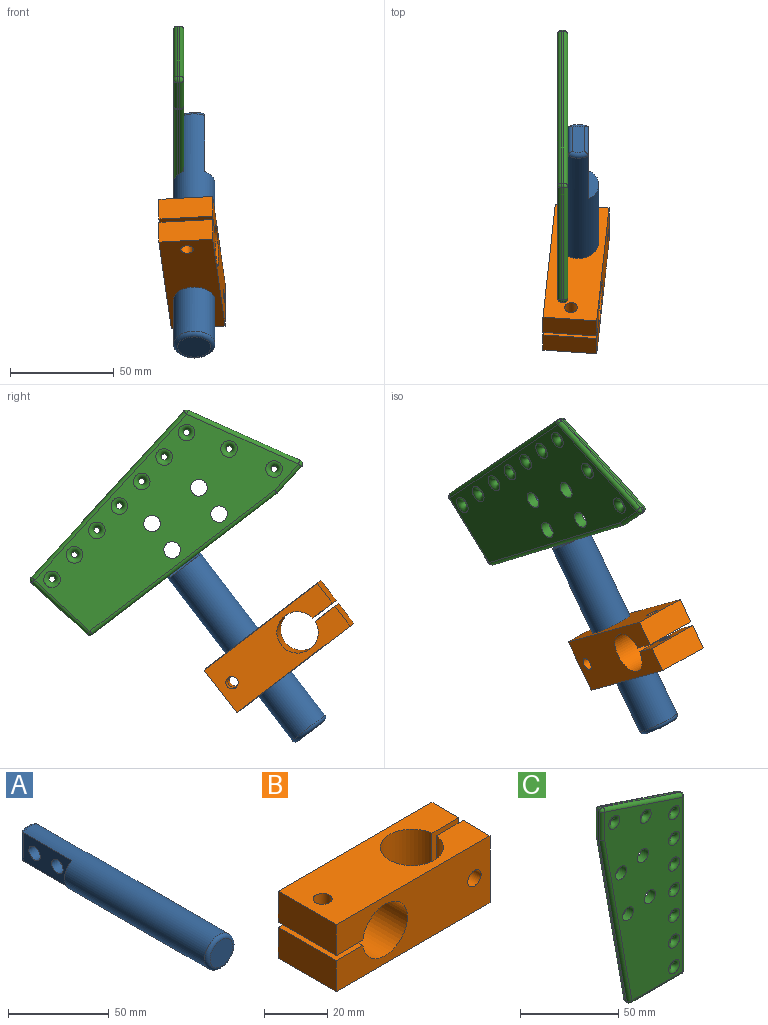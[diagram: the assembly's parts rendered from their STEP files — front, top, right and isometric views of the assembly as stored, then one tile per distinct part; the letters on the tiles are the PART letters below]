
ASSEMBLY  parts=3 mates=2
PART A: 14 faces, bbox 21.6x136x21.6 mm
  f0: plane 17.32x5mm, normal (0,1,0), area 61.4mm2, adj f1,f5
  f1: cylinder r=10mm len=132mm, axis (0,1,0), area 6869.6mm2, adj f0,f3,f4,f5,f9,f12,f13
  f2: plane 16x16mm, normal (0,-1,0), area 201.1mm2, adj f13
  f3: plane 17.32x5mm, normal (0,1,0), area 61.4mm2, adj f1,f4
  f4: plane 34x17.32mm, normal (-1,0,0), area 488.4mm2, adj f1,f3,f7,f8,f10
  f5: plane 34x17.32mm, normal (1,0,0), area 488.4mm2, adj f0,f1,f7,f8,f11
  f6: plane 16x6mm, normal (0,1,0), area 93.7mm2, adj f9,f10,f11,f12
  f7: cylinder r=4mm len=10mm, axis (-1,0,0), area 251.3mm2, adj f4,f5
  f8: cylinder r=4mm len=10mm, axis (-1,0,0), area 251.3mm2, adj f4,f5
  f9: torus R=8mm, axis (0,-1,0), area 27.9mm2, adj f1,f6,f10,f11
  f10: cylinder r=2mm len=17.32mm, axis (0,0,1), area 51.7mm2, adj f4,f6,f9,f12
  f11: cylinder r=2mm len=17.32mm, axis (0,0,-1), area 51.7mm2, adj f5,f6,f9,f12
  f12: torus R=8mm, axis (0,-1,0), area 27.9mm2, adj f1,f6,f10,f11
  f13: torus R=8mm, axis (0,-1,0), area 183mm2, adj f1,f2
PART B: 18 faces, bbox 69x26x26 mm
  f0: plane 26x12mm, normal (1,0,0), area 312mm2, adj f2,f8,f11,f15
  f1: cylinder r=3mm len=12mm, axis (0,1,0), area 226.2mm2, adj f11,f15
  f2: plane 69x26mm, normal (0,0,1), area 1427.5mm2, adj f0,f3,f9,f11,f12,f13,f14,f15
  f3: plane 26x12mm, normal (-1,0,0), area 312mm2, adj f2,f4,f11,f12
  f4: plane 26x12.05mm, normal (0,0,-1), area 285mm2, adj f3,f5,f11,f12,f17
  f5: cylinder r=10mm len=26mm, axis (0,1,0), area 1581.5mm2, adj f4,f6,f11,f12
  f6: plane 26x12.05mm, normal (0,0,1), area 285mm2, adj f5,f7,f11,f12,f16
  f7: plane 26x12mm, normal (-1,0,0), area 312mm2, adj f6,f8,f11,f12
  f8: plane 69x26mm, normal (0,0,-1), area 1427.5mm2, adj f0,f7,f9,f11,f12,f13,f14,f15
  f9: plane 26x12mm, normal (1,0,0), area 312mm2, adj f2,f8,f12,f14
  f10: cylinder r=3mm len=12mm, axis (0,1,0), area 226.2mm2, adj f12,f14
  f11: plane 69x26mm, normal (0,-1,0), area 1427.5mm2, adj f0,f1,f2,f3,f4,f5,f6,f7
  f12: plane 69x26mm, normal (0,1,0), area 1427.5mm2, adj f2,f3,f4,f5,f6,f7,f8,f9
  f13: cylinder r=10mm len=26mm, axis (0,0,1), area 1581.5mm2, adj f2,f8,f14,f15
  f14: plane 26x12.05mm, normal (0,-1,0), area 285mm2, adj f2,f8,f9,f10,f13
  f15: plane 26x12.05mm, normal (0,1,0), area 285mm2, adj f0,f1,f2,f8,f13
  f16: cylinder r=3mm len=12mm, axis (0,0,1), area 226.2mm2, adj f6,f8
  f17: cylinder r=3mm len=12mm, axis (0,0,1), area 226.2mm2, adj f2,f4
PART C: 45 faces, bbox 60x5x131.2 mm
  f0: plane 108.56x1mm, normal (1,0,0), area 108.6mm2, adj f20,f21,f22,f23
  f1: plane 56x18.67mm, normal (0.32,0,0.95), area 59mm2, adj f23,f28,f32,f33
  f2: plane 17.05x1mm, normal (-1,0,0), area 17mm2, adj f33,f38,f41,f44
  f3: plane 110.18x19.67mm, normal (-0.98,0,-0.18), area 111.9mm2, adj f30,f39,f40,f44
  f4: cylinder r=4mm len=8mm, axis (0,1,0), area 125.7mm2, adj f9,f10
  f5: cylinder r=4mm len=8mm, axis (0,1,0), area 125.7mm2, adj f9,f10
  f6: cylinder r=4mm len=8mm, axis (0,1,0), area 125.7mm2, adj f9,f10
  f7: cylinder r=4mm len=8mm, axis (0,1,0), area 125.7mm2, adj f9,f10
  f8: plane 36.33x1mm, normal (0,0,-1), area 36.3mm2, adj f21,f29,f30,f31
  f9: plane 127.23x56mm, normal (0,-1,0), area 4864.7mm2, adj f4,f5,f6,f7,f11,f12,f13,f14
  f10: plane 127.23x56mm, normal (0,1,0), area 4864.7mm2, adj f4,f5,f6,f7,f11,f12,f13,f14
  f11: torus R=4mm, axis (0,-1,0), area 118.9mm2, adj f9,f10
  f12: torus R=4mm, axis (0,-1,0), area 118.9mm2, adj f9,f10
  f13: torus R=4mm, axis (0,-1,0), area 118.9mm2, adj f9,f10
  f14: torus R=4mm, axis (0,-1,0), area 118.9mm2, adj f9,f10
  f15: torus R=4mm, axis (0,-1,0), area 118.9mm2, adj f9,f10
  f16: torus R=4mm, axis (0,-1,0), area 118.9mm2, adj f9,f10
  f17: torus R=4mm, axis (0,-1,0), area 118.9mm2, adj f9,f10
  f18: torus R=4mm, axis (0,-1,0), area 118.9mm2, adj f9,f10
  f19: torus R=4mm, axis (0,-1,0), area 118.9mm2, adj f9,f10
  f20: cylinder r=2mm len=108.56mm, axis (0,0,-1), area 341mm2, adj f0,f9,f24,f25
  f21: cylinder r=2mm len=2mm, axis (0,-1,0), area 3.1mm2, adj f0,f8,f25,f26
  f22: cylinder r=2mm len=108.56mm, axis (0,0,1), area 341mm2, adj f0,f10,f26,f27
  f23: cylinder r=2mm len=1.9mm, axis (0,1,0), area 2.5mm2, adj f0,f1,f24,f27
  f24: sphere r=2mm, area 5mm2, adj f20,f23,f28
  f25: sphere r=2mm, area 6.3mm2, adj f20,f21,f29
  f26: sphere r=2mm, area 6.3mm2, adj f21,f22,f31
  f27: sphere r=2mm, area 5mm2, adj f22,f23,f32
  f28: cylinder r=2mm len=56.63mm, axis (0.95,0,-0.32), area 185.4mm2, adj f1,f9,f24,f34
  f29: cylinder r=2mm len=36.33mm, axis (-1,0,0), area 114.1mm2, adj f8,f9,f25,f35
  f30: cylinder r=2mm len=1.97mm, axis (0,1,0), area 2.8mm2, adj f3,f8,f35,f36
  f31: cylinder r=2mm len=36.33mm, axis (1,0,0), area 114.1mm2, adj f8,f10,f26,f36
  f32: cylinder r=2mm len=56.63mm, axis (-0.95,0,0.32), area 185.4mm2, adj f1,f10,f27,f37
  f33: cylinder r=2mm len=2.63mm, axis (0,1,0), area 3.8mm2, adj f1,f2,f34,f37
  f34: sphere r=2mm, area 7.6mm2, adj f28,f33,f38
  f35: sphere r=2mm, area 5.6mm2, adj f29,f30,f39
  f36: sphere r=2mm, area 5.6mm2, adj f30,f31,f40
  f37: sphere r=2mm, area 7.6mm2, adj f32,f33,f41
  f38: cylinder r=2mm len=17.05mm, axis (0,0,1), area 53.6mm2, adj f2,f9,f34,f42
  f39: cylinder r=2mm len=110.53mm, axis (-0.18,0,0.98), area 351.6mm2, adj f3,f9,f35,f42
  f40: cylinder r=2mm len=110.53mm, axis (0.18,0,-0.98), area 351.6mm2, adj f3,f10,f36,f43
  f41: cylinder r=2mm len=17.05mm, axis (0,0,-1), area 53.6mm2, adj f2,f10,f37,f43
  f42: sphere r=2mm, area 0.7mm2, adj f38,f39,f44
  f43: sphere r=2mm, area 0.7mm2, adj f40,f41,f44
  f44: cylinder r=2mm len=1mm, axis (0,-1,0), area 0.4mm2, adj f2,f3,f42,f43
PLACE A rot(axis=(1,0,0),52.5deg) t=(62.53,113.22,-31.84)mm
PLACE B rot(axis=(-0.33,0.3,0.89),91.5deg) t=(45.53,49.38,-39.97)mm
PLACE C rot(axis=(0.34,-0.34,0.88),97.6deg) t=(52.53,68.63,3.46)mm fixed
MATE revolute C.f6 <-> A.f7  axis (-1,0,0) through (52.53,119.3,-23.91)mm
MATE cylindrical B.f13 <-> A.f1  axis (0,0.61,0.79) through (62.53,85.65,-67.79)mm
